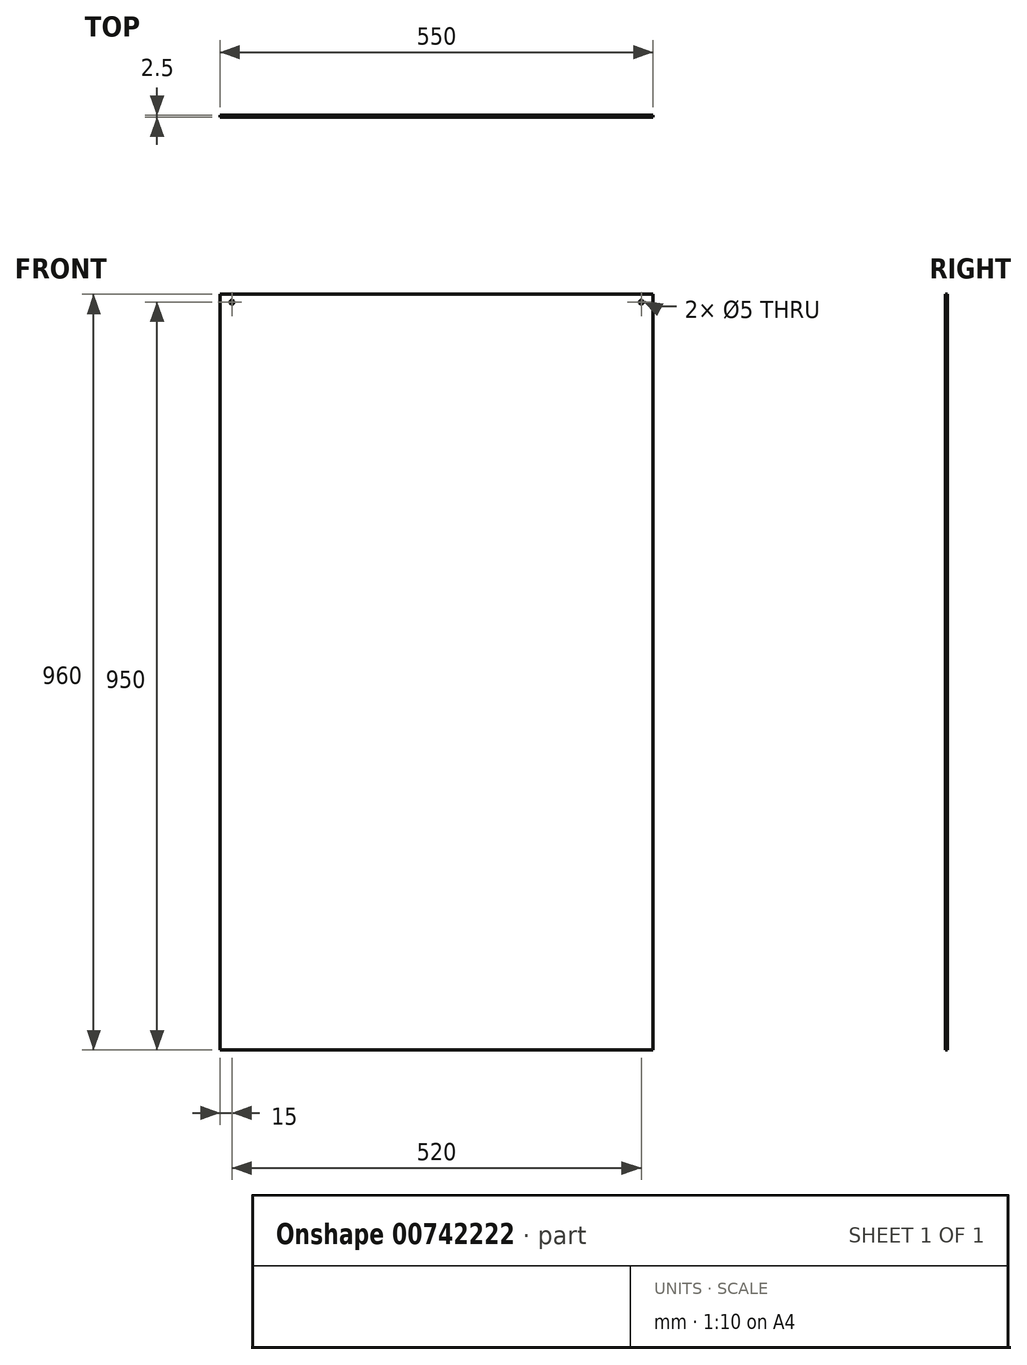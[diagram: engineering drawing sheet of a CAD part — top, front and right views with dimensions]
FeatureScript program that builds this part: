
annotation { "Feature Type Name" : "Feature", "Feature Type Description" : "" }
export const myFeature = defineFeature(function(context is Context, id is Id, definition is map)
    precondition{}
    {
        {
            var Q0;
            Q0=qCreatedBy(makeId("Front.planeOp"),FACE);
            var sketch = newSketch(context, id + "F0", { "sketchPlane" : qUnion([Q0])});
            skLineSegment(sketch, "E0.bottom", {"start": v(-275, 480) * mm, "end": v(275, 480) * mm});
            skLineSegment(sketch, "E0.top", {"start": v(-275, -480) * mm, "end": v(275, -480) * mm});
            skLineSegment(sketch, "E0.left", {"start": v(-275, 480) * mm, "end": v(-275, -480) * mm});
            skLineSegment(sketch, "E0.right", {"start": v(275, 480) * mm, "end": v(275, -480) * mm});
            skSolve(sketch);
        }
        {
            var Q0;
            Q0 = qSketchRegion(id + "F0", true);
            extrude(context, id + "F1", {"entities" : qUnion([Q0]), "depth" : 2.5 * mm, "offsetDistance" : 25 * mm});
        }
        {
            var Q0;
            Q0=makeQuery(id+"F1.opExtrude","CAP_FACE",FACE,{"disambiguationData":[OSD([sQuery(id+"F0.wireOp",EDGE,"E0.bottom"),sQuery(id+"F0.wireOp",EDGE,"E0.top"),sQuery(id+"F0.wireOp",EDGE,"E0.left"),sQuery(id+"F0.wireOp",EDGE,"E0.right")])],"isStart":false});
            var sketch = newSketch(context, id + "F2", { "sketchPlane" : qUnion([Q0])});
            skCircle(sketch, "E1", {"center": v(-177.89, 116.93) * mm, "radius": 5 * mm});
            skCircle(sketch, "E2", {"center": v(35, 116.93) * mm, "radius": 5 * mm});
            skCircle(sketch, "E3", {"center": v(-165, -83.07) * mm, "radius": 5 * mm});
            skCircle(sketch, "E4", {"center": v(35, -83.07) * mm, "radius": 5 * mm});
            skSolve(sketch);
        }
        {
            var Q0;
            Q0=makeQuery(id+"F2.imprint","IMPRINT",FACE,{"disambiguationData":[TD([[makeQuery(id+"F2.imprint","IMPRINT",EDGE,{"derivedFrom":sQuery(id+"F2.wireOp",EDGE,"E1")}),-1.0]])]});
            var sketch = newSketch(context, id + "F3", { "sketchPlane" : qUnion([Q0])});
            skCircle(sketch, "E5", {"center": v(-260, 470) * mm, "radius": 2.5 * mm});
            skCircle(sketch, "E6", {"center": v(260, 470) * mm, "radius": 2.5 * mm});
            skSolve(sketch);
        }
        {
            var Q0;
            Q0 = qSketchRegion(id + "F3", true);
            extrude(context, id + "F4", {"entities" : qUnion([Q0]), "operationType" : NewBodyOperationType.REMOVE, "endBound" : BoundingType.THROUGH_ALL, "oppositeDirection" : true, "depth" : 25 * mm, "offsetDistance" : 25 * mm});
        }
    });
